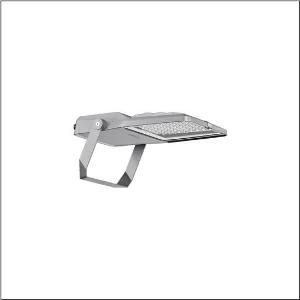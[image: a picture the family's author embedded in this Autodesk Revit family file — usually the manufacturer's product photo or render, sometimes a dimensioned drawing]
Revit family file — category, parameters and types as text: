
# Revit family: floodlight_fl_21_iq_mini___pl33t_5xa7772b2f1a_bcb0
name_source: partatom
category: Lighting Fixtures
units: mm (PartAtom-declared; Revit-internal decimal feet)

## family parameters
Cut with Voids When Loaded = No
Host = Face
Light Source = No
Part Type = Normal
Room Calculation Point = No
Round Connector Dimension = Use Diameter
Shared = No

## types (1)
- --- (1 x LED, 6170 lm, 45.5 W, 3000K)
    Apparent Load = 46 VA
    CIE Flux Codes = 26 75 99 100 100
    Color Rendering = 70
    Color Temperature = 3000K
    Default Elevation = 1800 mm
    Description = Floodlight FL 21 iQ mini, floodlight, primary light control with lens, of PMMA, primary optical cover: protective disc, of toughened safety glass, transparent, light distribution: PL33T, light emission: direct distribution, installation type: surface-mounted, LED, High Power LED, rated luminous flux: 6.170lm, luminous efficacy: 136lm/W, light colour: 730, colour temperature: 3000K, control: Street-Remote, Auto-Match, Temp-Guard, Night-Set, Smart-Wire, Desk-Remote (wireless, voltage-free reading and setting of iQ features in the workshop via application-optimized NFC function/RFID function), optimised constant luminous flux control (CLO 2.0), with terminal, 6-pole, mains connection: 220..240V, AC, 50/60Hz, start of lifetime: 46W, end of service life: 48W, reduction: 22W, luminaire housing, of diecast aluminium, powder-coated, Siteco® metallic grey (DB 702S), corrosivity category C5 mid according to DIN EN ISO 12944, sealing non-destructively replaceable, mounting bracket, of steel, galvanised, powder-coated, Siteco® metallic grey (DB 702S), protection rating (complete): IP66, insulation class (complete): insulation class II (safety insulation), certification: CE, ENEC, VDE, protection symbol: D, impact resistance: IK08, permissible operating ambient temperature: -40..+40°C, permissible operating ambient temperature for outdoor applications: -40..+50°C, standard: DIN EN 12944, LABS conformity tested according to VDMA 24364:2018-05, packaging unit: 1 piece

Light Distribution: PL33T
    Height = 70 mm
    Lamp = 1 x LED
    Lamp Light Flux = 6170 lm
    Lamp Power = 45.5 W
    Lamp count = 1
    Length = 485 mm
    Luminous efficacy = 136 lm/W
    Manufacturer = Siteco
    ModVariant = No
    Model = 5XA7772B2F1A
    Number of Poles = 1
    OnlyDefault = Yes
    Power Factor = 1
    Product Name = Floodlight FL 21 iQ mini | PL33T
    Product group = floodlight | pylon annexe
    ProductGroupID = 6200
    Protection Class = Protection class II
    Protection Degree = IP 66
    RLX_Detail_Level = 1
    RLX_Emergency_Light_Flux = 0 lm
    RLX_Emergency_Type = 0
    RLX_Emergency_Type_DB = No
    RlxData = <blob elided: 96189 chars, md5=72bbe95d>
    Socket = socket
    Standby Power = 0 W
    System Light Flux = 6170 lm
    System Power = 46 W
    Type Comments = factory setting: luminous flux: 100 % | dim-lin: 254 | 463 mA
    Type Image = l_1006845.jpg
    URL = http://relux.com
    VarID = @adj_082587
    Voltage = 0 V
    Weight = 0.00 kg
    Width = 337 mm

## geometry (parser evidence)
native form markers: Blend x4, Sweep x13
no freeform markers — native parametric forms only
